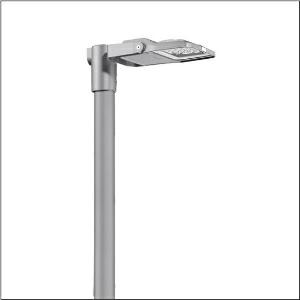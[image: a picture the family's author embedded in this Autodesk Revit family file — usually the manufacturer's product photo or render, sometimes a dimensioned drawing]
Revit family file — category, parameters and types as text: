
# Revit family: floodlight_fl_21_iq_micro___pl52_5xa7761a2d3a_8ecb
name_source: partatom
category: Lighting Fixtures
units: mm (PartAtom-declared; Revit-internal decimal feet)

## family parameters
Cut with Voids When Loaded = No
Host = Face
Light Source = No
Part Type = Normal
Room Calculation Point = No
Round Connector Dimension = Use Diameter
Shared = No

## types (1)
- --- (1 x LED, 2890 lm, 23.1 W, 3000K)
    Apparent Load = 23 VA
    CIE Flux Codes = 26 60 98 100 100
    Color Rendering = 70
    Color Temperature = 3000K
    Default Elevation = 1800 mm
    Description = Floodlight FL 21 iQ micro, floodlight, primary light control with lens, of PMMA, primary optical cover: protective disc, of toughened safety glass, transparent, light distribution: PL52, light emission: direct distribution, installation type: surface-mounted, LED, High Power LED, rated luminous flux: 2.890lm, luminous efficacy: 125lm/W, light colour: 730, colour temperature: 3000K, control: optimised constant luminous flux control (CLO 2.0), Desk-Remote (wireless, voltage-free reading and setting of iQ features in the workshop via application-optimized NFC function/RFID function), Light-Fading, Smart-Wire, Night-Set, Lumen-Switch, Temp-Guard, Auto-Match, with terminal, 6-pole, mains connection: 220..240V, AC, 50/60Hz, start of lifetime: 23W, end of service life: 24W, reduction: 11W, luminaire housing, of diecast aluminium, powder-coated, Siteco® metallic grey (DB 702S), corrosivity category C5 mid according to DIN EN ISO 12944, sealing non-destructively replaceable, please order mast flange separately, mast bracket, of steel, galvanised, powder-coated, Siteco® metallic grey (DB 702S), protection rating (complete): IP66, insulation class (complete): insulation class II (safety insulation), certification: CE, ENEC, VDE, protection symbol: D, impact resistance: IK07, permissible operating ambient temperature: -40..+40°C, permissible operating ambient temperature for outdoor applications: -40..+50°C, standard: DIN EN 12944, LABS conformity tested according to VDMA 24364:2018-05, packaging unit: 1 piece

Light Distribution: PL52
    Height = 65 mm
    Lamp = 1 x LED
    Lamp Light Flux = 2890 lm
    Lamp Power = 23.1 W
    Lamp count = 1
    Length = 312 mm
    Luminous efficacy = 125 lm/W
    Manufacturer = Siteco
    ModVariant = No
    Model = 5XA7761A2D3A
    Number of Poles = 1
    OnlyDefault = Yes
    Power Factor = 1
    Product Name = Floodlight FL 21 iQ micro | PL52
    Product group = floodlight | pylon top
    ProductGroupID = 6101
    Protection Class = Protection class II
    Protection Degree = IP 66
    RLX_Detail_Level = 1
    RLX_Emergency_Light_Flux = 0 lm
    RLX_Emergency_Type = 0
    RLX_Emergency_Type_DB = No
    RlxData = <blob elided: 101889 chars, md5=0aec40c1>
    Socket = socket
    Standby Power = 0 W
    System Light Flux = 2890 lm
    System Power = 23 W
    Type Comments = factory setting: luminous flux: 100 % | dim-lin: 254 | 455 mA
    Type Image = l_1007121.jpg
    URL = http://relux.com
    VarID = @adj_110885
    Voltage = 0 V
    Weight = 0.00 kg
    Width = 230 mm

## geometry (parser evidence)
native form markers: Blend x4, Sweep x13
no freeform markers — native parametric forms only
